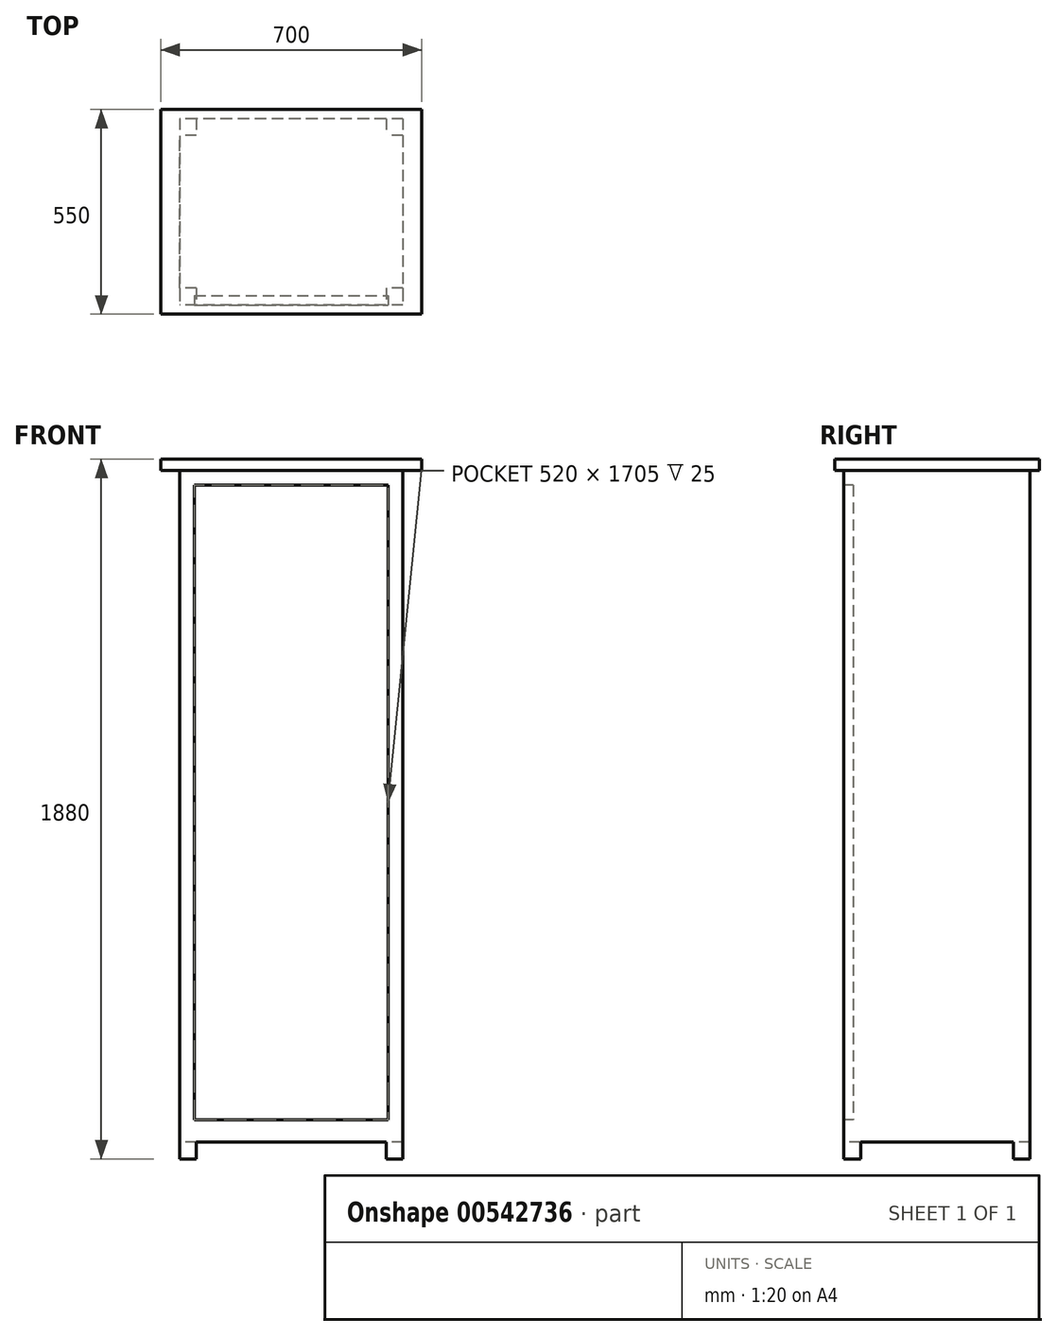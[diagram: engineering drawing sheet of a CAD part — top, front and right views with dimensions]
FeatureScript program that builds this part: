
annotation { "Feature Type Name" : "Feature", "Feature Type Description" : "" }
export const myFeature = defineFeature(function(context is Context, id is Id, definition is map)
    precondition{}
    {
        {
            var Q0;
            Q0=qCreatedBy(makeId("Top.planeOp"),FACE);
            var sketch = newSketch(context, id + "F0", { "sketchPlane" : qUnion([Q0])});
            skLineSegment(sketch, "E0.bottom", {"start": v(300, 250) * mm, "end": v(-300, 250) * mm});
            skLineSegment(sketch, "E0.top", {"start": v(300, -250) * mm, "end": v(-300, -250) * mm});
            skLineSegment(sketch, "E0.left", {"start": v(300, 250) * mm, "end": v(300, -250) * mm});
            skLineSegment(sketch, "E0.right", {"start": v(-300, 250) * mm, "end": v(-300, -250) * mm});
            skPoint(sketch, "E0.middle", {"position": v(0, 0) * mm});
            skSolve(sketch);
        }
        {
            var Q0;
            Q0 = qSketchRegion(id + "F0", true);
            extrude(context, id + "F1", {"entities" : qUnion([Q0]), "depth" : 1850 * mm, "offsetDistance" : 25 * mm});
        }
        {
            var Q0;
            Q0=makeQuery(id+"F1.opExtrude","CAP_FACE",FACE,{"disambiguationData":[OSD([sQuery(id+"F0.wireOp",EDGE,"E0.bottom"),sQuery(id+"F0.wireOp",EDGE,"E0.top"),sQuery(id+"F0.wireOp",EDGE,"E0.left"),sQuery(id+"F0.wireOp",EDGE,"E0.right")])],"isStart":false});
            var sketch = newSketch(context, id + "F2", { "sketchPlane" : qUnion([Q0])});
            skLineSegment(sketch, "E1.bottom", {"start": v(350, 275) * mm, "end": v(-350, 275) * mm});
            skLineSegment(sketch, "E1.top", {"start": v(350, -275) * mm, "end": v(-350, -275) * mm});
            skLineSegment(sketch, "E1.left", {"start": v(350, 275) * mm, "end": v(350, -275) * mm});
            skLineSegment(sketch, "E1.right", {"start": v(-350, 275) * mm, "end": v(-350, -275) * mm});
            skPoint(sketch, "E1.middle", {"position": v(0, 0) * mm});
            skSolve(sketch);
        }
        {
            var Q0;
            Q0 = qSketchRegion(id + "F2", true);
            extrude(context, id + "F3", {"entities" : qUnion([Q0]), "operationType" : NewBodyOperationType.ADD, "depth" : 30 * mm, "offsetDistance" : 25 * mm});
        }
        {
            var Q0;
            Q0=makeQuery(id+"F1.opExtrude","SWEPT_FACE",FACE,{"disambiguationData":[OSD([sQuery(id+"F0.wireOp",EDGE,"E0.top")])]});
            var sketch = newSketch(context, id + "F4", { "sketchPlane" : qUnion([Q0])});
            skLineSegment(sketch, "E2.bottom", {"start": v(-255, 0) * mm, "end": v(255, 0) * mm});
            skLineSegment(sketch, "E2.top", {"start": v(-255, 45) * mm, "end": v(255, 45) * mm});
            skLineSegment(sketch, "E2.left", {"start": v(-255, 0) * mm, "end": v(-255, 45) * mm});
            skLineSegment(sketch, "E2.right", {"start": v(255, 0) * mm, "end": v(255, 45) * mm});
            skPoint(sketch, "E2.middle", {"position": v(0, 22.5) * mm});
            skSolve(sketch);
        }
        {
            var Q0;
            Q0 = qSketchRegion(id + "F4", true);
            extrude(context, id + "F5", {"entities" : qUnion([Q0]), "operationType" : NewBodyOperationType.REMOVE, "endBound" : BoundingType.UP_TO_NEXT, "oppositeDirection" : true, "depth" : 25 * mm, "offsetDistance" : 25 * mm});
        }
        {
            var Q0;
            Q0=makeQuery(id+"F1.opExtrude","SWEPT_FACE",FACE,{"disambiguationData":[OSD([sQuery(id+"F0.wireOp",EDGE,"E0.right")])]});
            var sketch = newSketch(context, id + "F6", { "sketchPlane" : qUnion([Q0])});
            skLineSegment(sketch, "E3.bottom", {"start": v(205, 0) * mm, "end": v(-205, 0) * mm});
            skLineSegment(sketch, "E3.top", {"start": v(205, 45) * mm, "end": v(-205, 45) * mm});
            skLineSegment(sketch, "E3.left", {"start": v(205, 0) * mm, "end": v(205, 45) * mm});
            skLineSegment(sketch, "E3.right", {"start": v(-205, 0) * mm, "end": v(-205, 45) * mm});
            skPoint(sketch, "E3.middle", {"position": v(0, 22.5) * mm});
            skSolve(sketch);
        }
        {
            var Q0;
            Q0 = qSketchRegion(id + "F6", true);
            extrude(context, id + "F7", {"entities" : qUnion([Q0]), "operationType" : NewBodyOperationType.REMOVE, "endBound" : BoundingType.THROUGH_ALL, "oppositeDirection" : true, "depth" : 25 * mm, "offsetDistance" : 25 * mm});
        }
        {
            var Q0;
            Q0=makeQuery(id+"F1.opExtrude","SWEPT_FACE",FACE,{"disambiguationData":[OSD([sQuery(id+"F0.wireOp",EDGE,"E0.top")])]});
            var sketch = newSketch(context, id + "F8", { "sketchPlane" : qUnion([Q0])});
            skLineSegment(sketch, "E4.bottom", {"start": v(-260, 1810) * mm, "end": v(260, 1810) * mm});
            skLineSegment(sketch, "E4.top", {"start": v(-260, 105) * mm, "end": v(260, 105) * mm});
            skLineSegment(sketch, "E4.left", {"start": v(-260, 1810) * mm, "end": v(-260, 105) * mm});
            skLineSegment(sketch, "E4.right", {"start": v(260, 1810) * mm, "end": v(260, 105) * mm});
            skPoint(sketch, "E4.middle", {"position": v(0, 957.5) * mm});
            skSolve(sketch);
        }
        {
            var Q0;
            Q0 = qSketchRegion(id + "F8", true);
            extrude(context, id + "F9", {"entities" : qUnion([Q0]), "operationType" : NewBodyOperationType.REMOVE, "oppositeDirection" : true, "depth" : 25 * mm, "offsetDistance" : 25 * mm});
        }
    });
